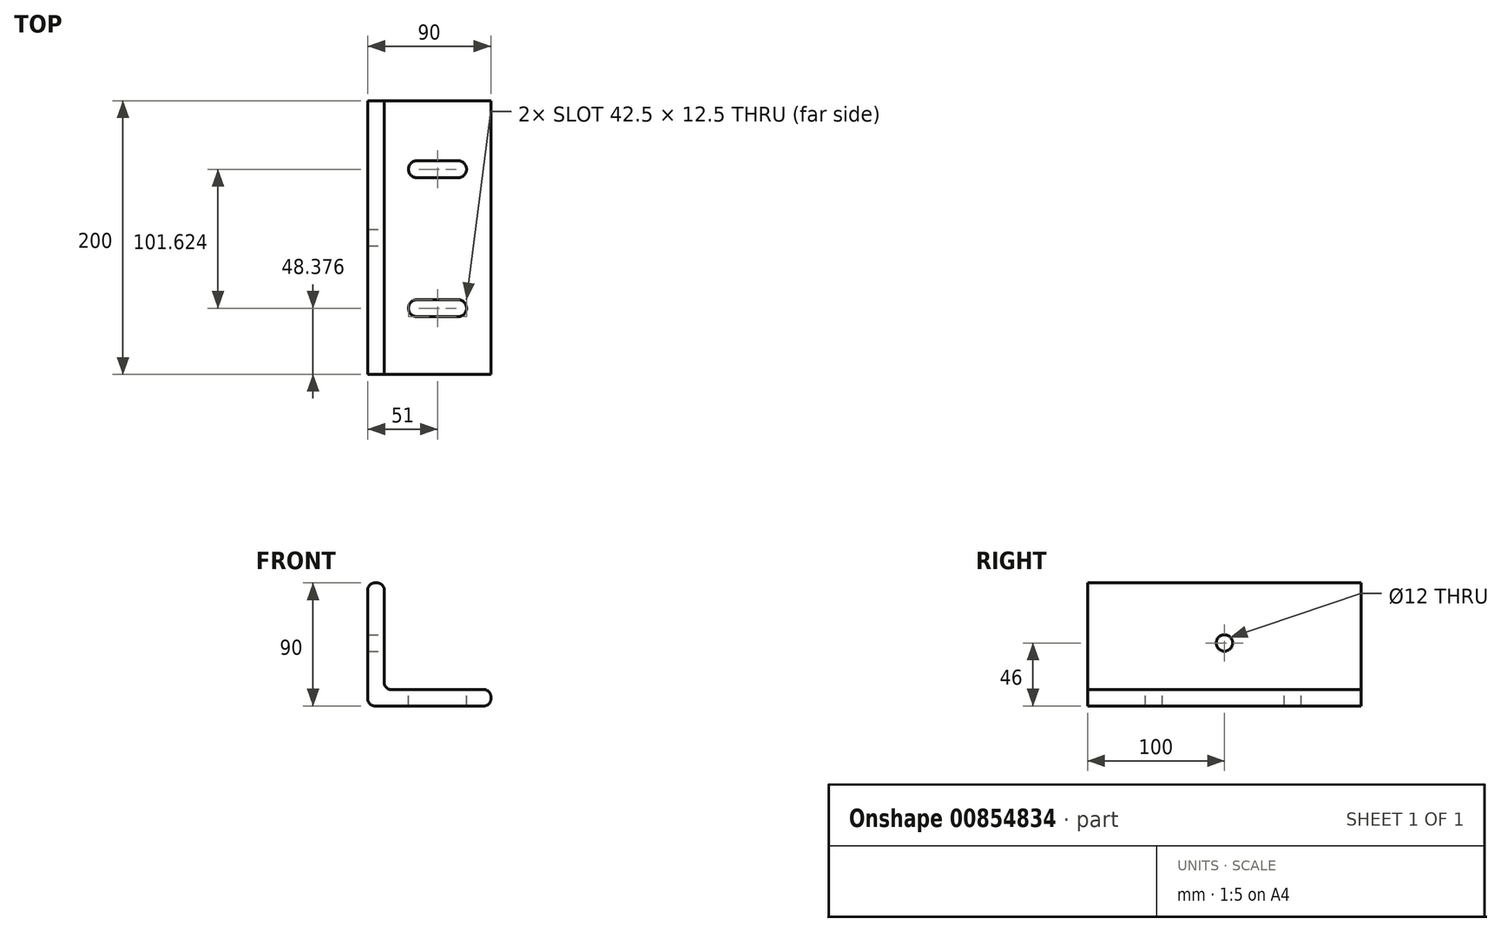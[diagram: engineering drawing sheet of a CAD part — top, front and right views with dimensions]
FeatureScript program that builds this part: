
annotation { "Feature Type Name" : "Feature", "Feature Type Description" : "" }
export const myFeature = defineFeature(function(context is Context, id is Id, definition is map)
    precondition{}
    {
        {
            var Q0;
            Q0=qCreatedBy(makeId("Front.planeOp"),FACE);
            var sketch = newSketch(context, id + "F0", { "sketchPlane" : qUnion([Q0])});
            skLineSegment(sketch, "E0", {"start": v(0, 0) * mm, "end": v(90, 0) * mm});
            skLineSegment(sketch, "E1", {"start": v(90, 0) * mm, "end": v(90, 12) * mm});
            skLineSegment(sketch, "E2", {"start": v(90, 12) * mm, "end": v(12, 12) * mm});
            skLineSegment(sketch, "E3", {"start": v(12, 12) * mm, "end": v(12, 90) * mm});
            skLineSegment(sketch, "E4", {"start": v(12, 90) * mm, "end": v(0, 90) * mm});
            skLineSegment(sketch, "E5", {"start": v(0, 90) * mm, "end": v(0, 0) * mm});
            skSolve(sketch);
        }
        {
            var Q0;
            Q0=makeQuery(id+"F0.imprint","IMPRINT",FACE,{"disambiguationData":[TD([[makeQuery(id+"F0.imprint","IMPRINT",EDGE,{"derivedFrom":sQuery(id+"F0.wireOp",EDGE,"E0")}),1.0]])]});
            extrude(context, id + "F1", {"entities" : qUnion([Q0]), "depth" : 200 * mm, "offsetDistance" : 25 * mm});
        }
        {
            var Q0;
            Q0=makeQuery(id+"F1.opExtrude","SWEPT_EDGE",EDGE,{"disambiguationData":[OSD([sQuery(id+"F0.wireOp",EDGE,"E3"),sQuery(id+"F0.wireOp",EDGE,"E4")])]});
            var Q1;
            Q1=makeQuery(id+"F1.opExtrude","SWEPT_EDGE",EDGE,{"disambiguationData":[OSD([sQuery(id+"F0.wireOp",EDGE,"E2"),sQuery(id+"F0.wireOp",EDGE,"E3")])]});
            var Q2;
            Q2=makeQuery(id+"F1.opExtrude","SWEPT_EDGE",EDGE,{"disambiguationData":[OSD([sQuery(id+"F0.wireOp",EDGE,"E1"),sQuery(id+"F0.wireOp",EDGE,"E2")])]});
            var Q3;
            Q3=makeQuery(id+"F1.opExtrude","SWEPT_EDGE",EDGE,{"disambiguationData":[OSD([sQuery(id+"F0.wireOp",EDGE,"E0"),sQuery(id+"F0.wireOp",EDGE,"E1")])]});
            var Q4;
            Q4=makeQuery(id+"F1.opExtrude","SWEPT_EDGE",EDGE,{"disambiguationData":[OSD([sQuery(id+"F0.wireOp",EDGE,"E4"),sQuery(id+"F0.wireOp",EDGE,"E5")])]});
            var Q5;
            Q5=makeQuery(id+"F1.opExtrude","SWEPT_EDGE",EDGE,{"disambiguationData":[OSD([sQuery(id+"F0.wireOp",EDGE,"E0"),sQuery(id+"F0.wireOp",EDGE,"E5")])]});
            fillet(context, id + "F2", {"entities" : qUnion([Q0, Q1, Q2, Q3, Q4, Q5]), "radius" : 5 * mm, "tangentPropagation" : true, "allowEdgeOverflow" : false});
        }
        {
            var Q0;
            Q0=makeQuery(id+"F1.opExtrude","SWEPT_FACE",FACE,{"disambiguationData":[OSD([sQuery(id+"F0.wireOp",EDGE,"E3")])]});
            var sketch = newSketch(context, id + "F3", { "sketchPlane" : qUnion([Q0])});
            skCircle(sketch, "E6", {"center": v(-100, 46) * mm, "radius": 6 * mm});
            skSolve(sketch);
        }
        {
            var Q0;
            Q0=makeQuery(id+"F3.imprint","IMPRINT",FACE,{"disambiguationData":[TD([[makeQuery(id+"F3.imprint","IMPRINT",EDGE,{"derivedFrom":sQuery(id+"F3.wireOp",EDGE,"E6")}),1.0]])]});
            extrude(context, id + "F4", {"entities" : qUnion([Q0]), "operationType" : NewBodyOperationType.REMOVE, "oppositeDirection" : true, "depth" : 25 * mm, "offsetDistance" : 25 * mm});
        }
        {
            var Q0;
            Q0=makeQuery(id+"F1.opExtrude","SWEPT_FACE",FACE,{"disambiguationData":[OSD([sQuery(id+"F0.wireOp",EDGE,"E2")])]});
            var sketch = newSketch(context, id + "F5", { "sketchPlane" : qUnion([Q0])});
            skLineSegment(sketch, "E7", {"start": v(36, -43.75) * mm, "end": v(66, -43.75) * mm});
            skArc(sketch, "E8", {"start": v(66, -56.25) * mm, "mid": v(72.25, -50) * mm, "end": v(66, -43.75) * mm});
            skLineSegment(sketch, "E9", {"start": v(66, -56.25) * mm, "end": v(36, -56.25) * mm});
            skArc(sketch, "E10", {"start": v(36, -43.75) * mm, "mid": v(29.75, -50) * mm, "end": v(36, -56.25) * mm});
            skLineSegment(sketch, "E11", {"start": v(36, -145.37) * mm, "end": v(66, -145.37) * mm});
            skLineSegment(sketch, "E12", {"start": v(36, -157.87) * mm, "end": v(66, -157.87) * mm});
            skArc(sketch, "E13", {"start": v(66, -157.87) * mm, "mid": v(72.25, -151.62) * mm, "end": v(66, -145.37) * mm});
            skArc(sketch, "E14", {"start": v(36, -145.37) * mm, "mid": v(29.75, -151.62) * mm, "end": v(36, -157.87) * mm});
            skSolve(sketch);
        }
        {
            var Q0;
            Q0=makeQuery(id+"F5.imprint","IMPRINT",FACE,{"disambiguationData":[TD([[makeQuery(id+"F5.imprint","IMPRINT",EDGE,{"derivedFrom":sQuery(id+"F5.wireOp",EDGE,"E11")}),-1.0]])]});
            var Q1;
            Q1=makeQuery(id+"F5.imprint","IMPRINT",FACE,{"disambiguationData":[TD([[makeQuery(id+"F5.imprint","IMPRINT",EDGE,{"derivedFrom":sQuery(id+"F5.wireOp",EDGE,"E7")}),-1.0]])]});
            extrude(context, id + "F6", {"entities" : qUnion([Q0, Q1]), "operationType" : NewBodyOperationType.REMOVE, "oppositeDirection" : true, "depth" : 25 * mm, "offsetDistance" : 25 * mm});
        }
    });
